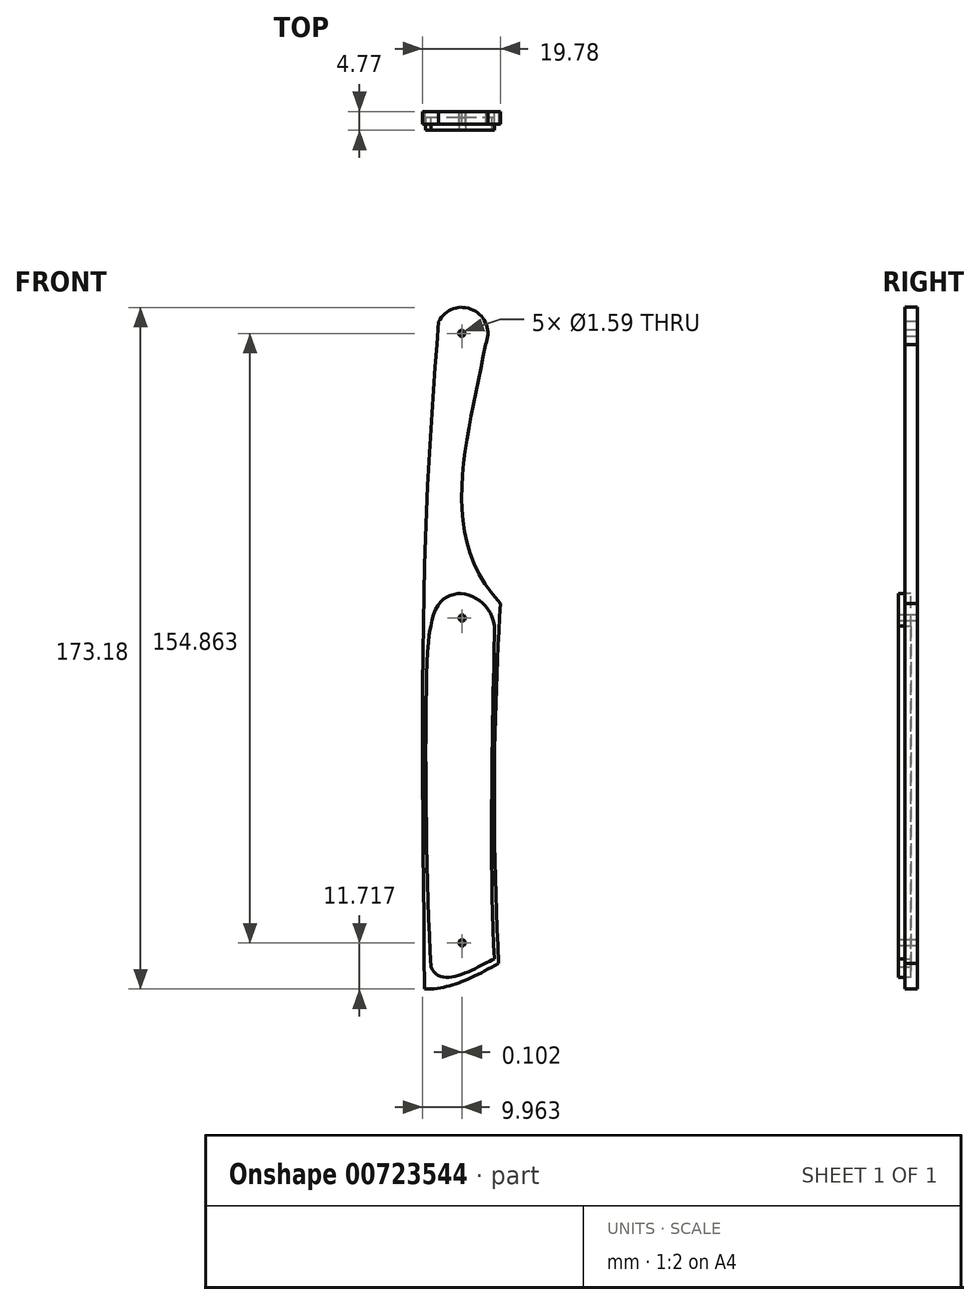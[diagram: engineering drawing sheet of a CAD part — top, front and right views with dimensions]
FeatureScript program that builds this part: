
annotation { "Feature Type Name" : "Feature", "Feature Type Description" : "" }
export const myFeature = defineFeature(function(context is Context, id is Id, definition is map)
    precondition{}
    {
        {
            var Q0;
            Q0=qCreatedBy(makeId("Front.planeOp"),FACE);
            var sketch = newSketch(context, id + "F0", { "sketchPlane" : qUnion([Q0])});
            skLineSegment(sketch, "E0.bottom", {"start": v(-37.67, 57.9) * mm, "end": v(-12.56, 57.9) * mm});
            skLineSegment(sketch, "E0.top", {"start": v(-37.67, -120.4) * mm, "end": v(-12.56, -120.4) * mm});
            skLineSegment(sketch, "E0.left", {"start": v(-37.67, 57.9) * mm, "end": v(-37.67, -120.4) * mm});
            skLineSegment(sketch, "E0.right", {"start": v(-12.56, 57.9) * mm, "end": v(-12.56, -120.4) * mm});
            skFitSpline(sketch, "E1", {"points": [v(-34.35, -116.48) * mm, v(-34.35, -7.97) * mm, v(-30.82, 53.02) * mm], "startDerivative": vector(-2.35, 203.54) * mm, "endDerivative": vector(10, 132.07) * mm});
            skArc(sketch, "E2", {"start": v(-18.94, 47.25) * mm, "mid": v(-22.02, 56.02) * mm, "end": v(-30.82, 53.02) * mm});
            skFitSpline(sketch, "E3", {"points": [v(-18.94, 47.25) * mm, v(-15.09, -18.56) * mm], "startDerivative": vector(-11.56, -69.34) * mm, "endDerivative": vector(51.04, -55.7) * mm});
            skFitSpline(sketch, "E4", {"points": [v(-15.53, -110) * mm, v(-15.09, -18.56) * mm], "startDerivative": vector(-5.54, 102.17) * mm, "endDerivative": vector(4.92, 79.65) * mm});
            skFitSpline(sketch, "E5", {"points": [v(-15.53, -110) * mm, v(-34.35, -116.48) * mm], "startDerivative": vector(-21.33, -11.64) * mm, "endDerivative": vector(-18.89, 0.78) * mm});
            skCircle(sketch, "E6", {"center": v(-24.9, 50.08) * mm, "radius": 0.8 * mm});
            skPoint(sketch, "E7", {"position": v(-24.9, 56.02) * mm});
            skPoint(sketch, "E7.positionSnap0", {"position": v(-22.02, 56.02) * mm});
            skPoint(sketch, "E8", {"position": v(-34.6, -18.56) * mm});
            skSolve(sketch);
        }
        {
            var Q0;
            Q0=makeQuery(id+"F0.imprint","IMPRINT",FACE,{"disambiguationData":[TD([[makeQuery(id+"F0.imprint","IMPRINT",EDGE,{"derivedFrom":sQuery(id+"F0.wireOp",EDGE,"E1")}),-1.0]])]});
            extrude(context, id + "F1", {"entities" : qUnion([Q0]), "endBound" : BoundingType.SYMMETRIC, "oppositeDirection" : true, "depth" : 3.17 * mm, "offsetDistance" : 25.4 * mm});
        }
        {
            var Q0;
            Q0=qCreatedBy(makeId("Front.planeOp"),FACE);
            var sketch = newSketch(context, id + "F2", { "sketchPlane" : qUnion([Q0])});
            skFitSpline(sketch, "E9", {"points": [v(-16.6, -108.9) * mm, v(-32.75, -110.87) * mm], "startDerivative": vector(-12.7, -5.56) * mm, "endDerivative": vector(-7.3, 18.53) * mm});
            skFitSpline(sketch, "E10", {"points": [v(-32.75, -110.87) * mm, v(-32.75, -24.26) * mm], "startDerivative": vector(-4.77, 85.78) * mm, "endDerivative": vector(5.78, 14.96) * mm});
            skFitSpline(sketch, "E11", {"points": [v(-32.75, -24.26) * mm, v(-16.6, -24.26) * mm], "startDerivative": vector(4.77, 38.13) * mm, "endDerivative": vector(3.97, -27) * mm});
            skFitSpline(sketch, "E12", {"points": [v(-16.6, -24.26) * mm, v(-16.6, -108.9) * mm], "startDerivative": vector(0, -24.2) * mm, "endDerivative": vector(5.05, -82) * mm});
            skSolve(sketch);
        }
        {
            var Q0;
            Q0=qSketchRegion(id+"F2",true);
            extrude(context, id + "F3", {"entities" : qUnion([Q0]), "depth" : 3.17 * mm, "offsetDistance" : 25.4 * mm});
        }
        {
            var Q0;
            Q0=makeQuery(id+"F1.opExtrude","CAP_FACE",FACE,{"disambiguationData":[OSD([sQuery(id+"F0.wireOp",EDGE,"E1"),sQuery(id+"F0.wireOp",EDGE,"E2"),sQuery(id+"F0.wireOp",EDGE,"E3"),sQuery(id+"F0.wireOp",EDGE,"E4"),sQuery(id+"F0.wireOp",EDGE,"E5"),sQuery(id+"F0.wireOp",EDGE,"E6")])],"isStart":false});
            var sketch = newSketch(context, id + "F4", { "sketchPlane" : qUnion([Q0])});
            skCircle(sketch, "E13", {"center": v(24.8, -22.25) * mm, "radius": 0.8 * mm});
            skCircle(sketch, "E14", {"center": v(24.81, -104.78) * mm, "radius": 0.8 * mm});
            skSolve(sketch);
        }
        {
            var Q0;
            Q0 = qSketchRegion(id + "F4", true);
            extrude(context, id + "F5", {"entities" : qUnion([Q0]), "operationType" : NewBodyOperationType.REMOVE, "endBound" : BoundingType.SYMMETRIC, "depth" : 25.4 * mm, "offsetDistance" : 25.4 * mm});
        }
    });
